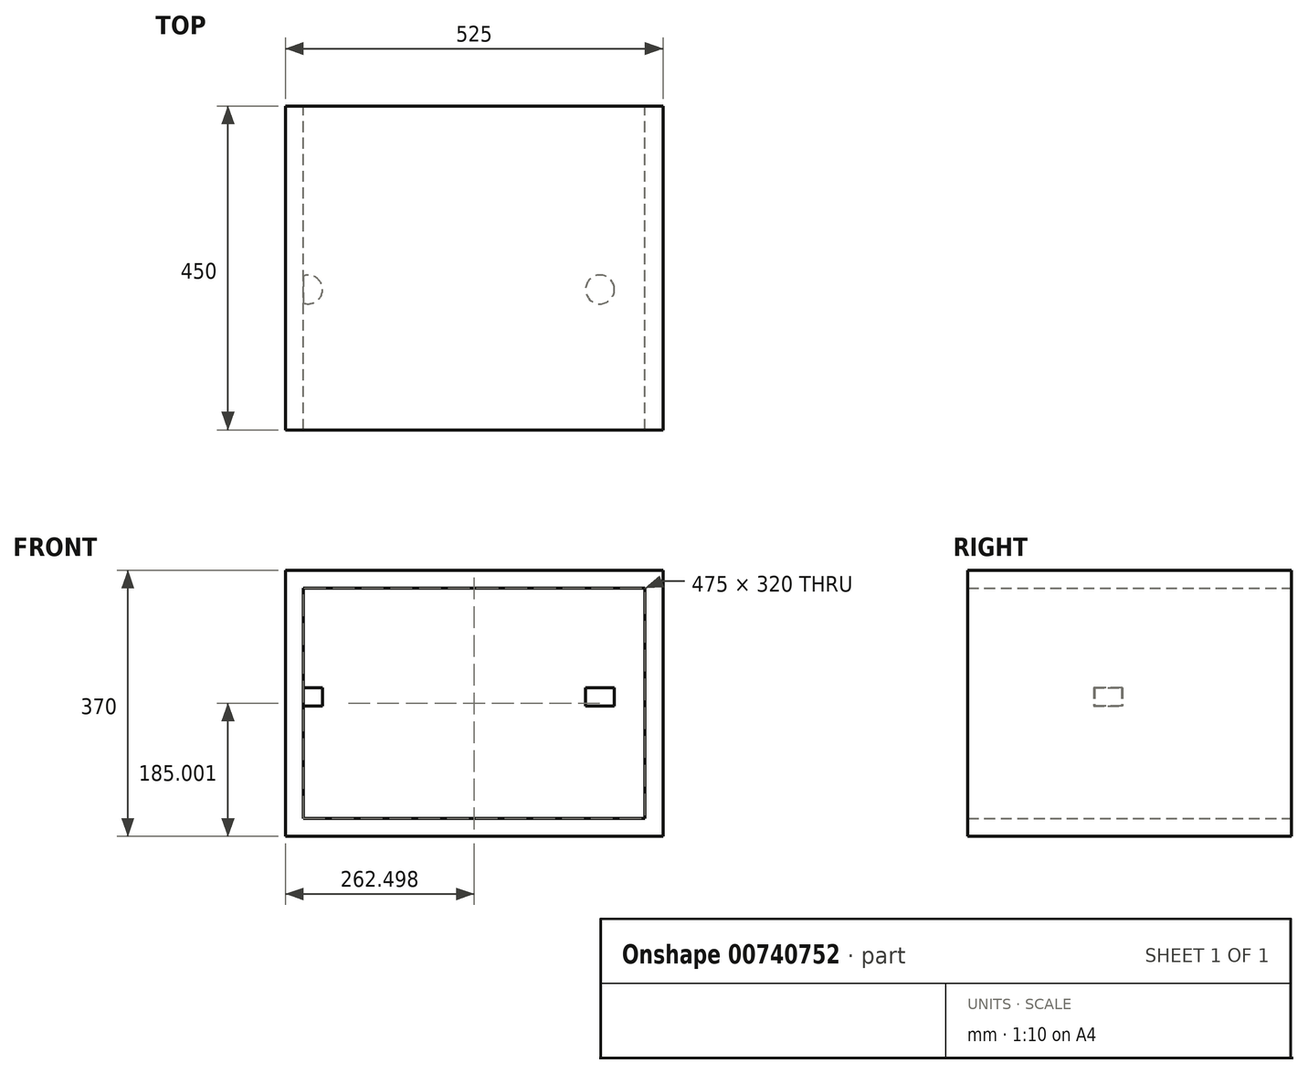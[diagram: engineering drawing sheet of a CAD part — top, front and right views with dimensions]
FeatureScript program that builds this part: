
annotation { "Feature Type Name" : "Feature", "Feature Type Description" : "" }
export const myFeature = defineFeature(function(context is Context, id is Id, definition is map)
    precondition{}
    {
        {
            var Q0;
            Q0=qCreatedBy(makeId("Front.planeOp"),FACE);
            var sketch = newSketch(context, id + "F0", { "sketchPlane" : qUnion([Q0])});
            skLineSegment(sketch, "E0.bottom", {"start": v(-374.33, 188.9) * mm, "end": v(150.67, 188.9) * mm});
            skLineSegment(sketch, "E0.top", {"start": v(-374.33, -181.1) * mm, "end": v(150.67, -181.1) * mm});
            skLineSegment(sketch, "E0.left", {"start": v(-374.33, 188.9) * mm, "end": v(-374.33, -181.1) * mm});
            skLineSegment(sketch, "E0.right", {"start": v(150.67, 188.9) * mm, "end": v(150.67, -181.1) * mm});
            skLineSegment(sketch, "E1.bottom", {"start": v(-349.33, 163.9) * mm, "end": v(125.67, 163.9) * mm});
            skLineSegment(sketch, "E1.top", {"start": v(-349.33, -156.1) * mm, "end": v(125.67, -156.1) * mm});
            skLineSegment(sketch, "E1.left", {"start": v(-349.33, 163.9) * mm, "end": v(-349.33, -156.1) * mm});
            skLineSegment(sketch, "E1.right", {"start": v(125.67, 163.9) * mm, "end": v(125.67, -156.1) * mm});
            skSolve(sketch);
        }
        {
            var Q0;
            Q0=makeQuery(id+"F0.imprint","IMPRINT",FACE,{"disambiguationData":[TD([[makeQuery(id+"F0.imprint","IMPRINT",EDGE,{"derivedFrom":sQuery(id+"F0.wireOp",EDGE,"E0.bottom")}),-1.0]])]});
            extrude(context, id + "F1", {"entities" : qUnion([Q0]), "depth" : 450 * mm, "offsetDistance" : 25.4 * mm});
        }
        {
            var Q0;
            Q0=qCreatedBy(makeId("Top.planeOp"),FACE);
            var sketch = newSketch(context, id + "F2", { "sketchPlane" : qUnion([Q0])});
            skLineSegment(sketch, "E2", {"start": v(-322.83, -254.86) * mm, "end": v(-362.83, -254.86) * mm});
            skCircle(sketch, "E3", {"center": v(-342.83, -254.86) * mm, "radius": 20 * mm});
            skCircle(sketch, "E4", {"center": v(63.1, -254.86) * mm, "radius": 20 * mm});
            skPoint(sketch, "E5.orphan", {"position": v(-424.95, 0) * mm});
            skPoint(sketch, "E6.orphan", {"position": v(172.59, 0) * mm});
            skLineSegment(sketch, "E7", {"start": v(63.1, -254.86) * mm, "end": v(83.1, -254.86) * mm});
            skSolve(sketch);
        }
        {
            var Q0;
            Q0 = qSketchRegion(id + "F2", true);
            extrude(context, id + "F3", {"entities" : qUnion([Q0]), "operationType" : NewBodyOperationType.ADD, "depth" : 25.4 * mm, "offsetDistance" : 25.4 * mm});
        }
    });
